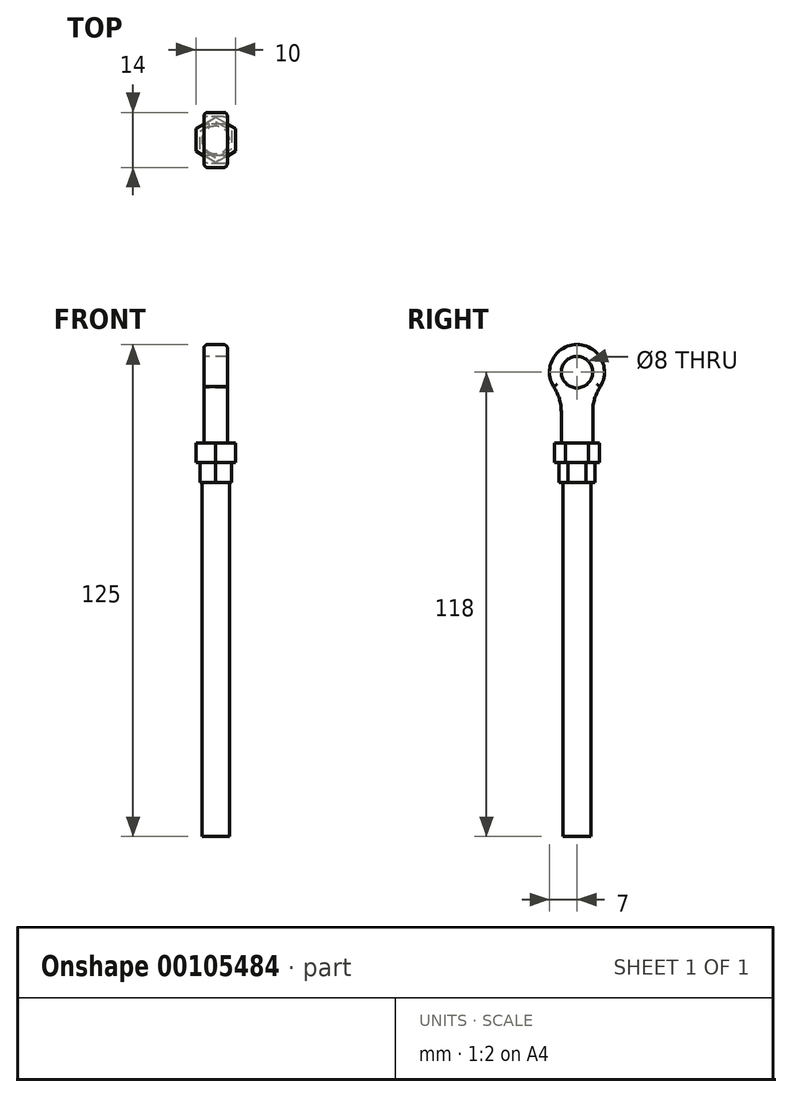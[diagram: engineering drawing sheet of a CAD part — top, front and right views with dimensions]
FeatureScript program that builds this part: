
annotation { "Feature Type Name" : "Feature", "Feature Type Description" : "" }
export const myFeature = defineFeature(function(context is Context, id is Id, definition is map)
    precondition{}
    {
        {
            var Q0;
            Q0=qCreatedBy(makeId("Top.planeOp"),FACE);
            var sketch = newSketch(context, id + "F0", { "sketchPlane" : qUnion([Q0])});
            skCircle(sketch, "E0", {"center": v(0, 0) * mm, "radius": 3.5 * mm});
            skSolve(sketch);
        }
        {
            var Q0;
            Q0=makeQuery(id+"F0.imprint","IMPRINT",FACE,{"disambiguationData":[TD([[makeQuery(id+"F0.imprint","IMPRINT",EDGE,{"derivedFrom":sQuery(id+"F0.wireOp",EDGE,"E0")}),1.0]])]});
            extrude(context, id + "F1", {"entities" : qUnion([Q0]), "depth" : 90 * mm});
        }
        {
            var Q0;
            Q0=makeQuery(id+"F1.opExtrude","CAP_FACE",FACE,{"disambiguationData":[OSD([sQuery(id+"F0.wireOp",EDGE,"E0")])],"isStart":false});
            var sketch = newSketch(context, id + "F2", { "sketchPlane" : qUnion([Q0])});
            skCircle(sketch, "E1.cCircle", {"center": v(0, 0) * mm, "radius": 4 * mm, "construction": true});
            skLineSegment(sketch, "E1.0", {"start": v(4, 2.3) * mm, "end": v(4, -2.3) * mm});
            skLineSegment(sketch, "E1.1", {"start": v(4, -2.3) * mm, "end": v(0, -4.62) * mm});
            skLineSegment(sketch, "E1.2", {"start": v(0, -4.62) * mm, "end": v(-4, -2.3) * mm});
            skLineSegment(sketch, "E1.3", {"start": v(-4, -2.3) * mm, "end": v(-4, 2.3) * mm});
            skLineSegment(sketch, "E1.4", {"start": v(-4, 2.3) * mm, "end": v(0, 4.62) * mm});
            skLineSegment(sketch, "E1.5", {"start": v(0, 4.62) * mm, "end": v(4, 2.3) * mm});
            skPoint(sketch, "E1.0.midPoint", {"position": v(4, 0) * mm});
            skSolve(sketch);
        }
        {
            var Q0;
            Q0 = qSketchRegion(id + "F2", true);
            extrude(context, id + "F3", {"entities" : qUnion([Q0]), "operationType" : NewBodyOperationType.ADD, "depth" : 5 * mm});
        }
        {
            var Q0;
            Q0=makeQuery(id+"F3.opExtrude","CAP_FACE",FACE,{"disambiguationData":[OSD([sQuery(id+"F2.wireOp",EDGE,"E1.0"),sQuery(id+"F2.wireOp",EDGE,"E1.1"),sQuery(id+"F2.wireOp",EDGE,"E1.2"),sQuery(id+"F2.wireOp",EDGE,"E1.3"),sQuery(id+"F2.wireOp",EDGE,"E1.4"),sQuery(id+"F2.wireOp",EDGE,"E1.5")])],"isStart":false});
            var sketch = newSketch(context, id + "F4", { "sketchPlane" : qUnion([Q0])});
            skCircle(sketch, "E2.cCircle", {"center": v(0, 0) * mm, "radius": 5 * mm, "construction": true});
            skLineSegment(sketch, "E2.0", {"start": v(5, 2.89) * mm, "end": v(5, -2.89) * mm});
            skLineSegment(sketch, "E2.1", {"start": v(5, -2.89) * mm, "end": v(0, -5.77) * mm});
            skLineSegment(sketch, "E2.2", {"start": v(0, -5.77) * mm, "end": v(-5, -2.89) * mm});
            skLineSegment(sketch, "E2.3", {"start": v(-5, -2.89) * mm, "end": v(-5, 2.89) * mm});
            skLineSegment(sketch, "E2.4", {"start": v(-5, 2.89) * mm, "end": v(0, 5.77) * mm});
            skLineSegment(sketch, "E2.5", {"start": v(0, 5.77) * mm, "end": v(5, 2.89) * mm});
            skPoint(sketch, "E2.0.midPoint", {"position": v(5, 0) * mm});
            skSolve(sketch);
        }
        {
            var Q0;
            Q0 = qSketchRegion(id + "F4", true);
            extrude(context, id + "F5", {"entities" : qUnion([Q0]), "operationType" : NewBodyOperationType.ADD, "depth" : 5 * mm});
        }
        {
            var Q0;
            Q0=qCreatedBy(makeId("Right.planeOp"),FACE);
            var sketch = newSketch(context, id + "F6", { "sketchPlane" : qUnion([Q0])});
            skLineSegment(sketch, "E3", {"start": v(0, 0) * mm, "end": v(0, 100) * mm});
            skArc(sketch, "E4", {"start": v(5.95, 114.3) * mm, "mid": v(0, 125) * mm, "end": v(-5.95, 114.3) * mm});
            skCircle(sketch, "E5", {"center": v(0, 118) * mm, "radius": 4 * mm});
            skLineSegment(sketch, "E6", {"start": v(0, 100) * mm, "end": v(-4, 100) * mm});
            skLineSegment(sketch, "E7", {"start": v(-4, 100) * mm, "end": v(-4, 108) * mm});
            skArc(sketch, "E8", {"start": v(-4, 108) * mm, "mid": v(-4.5, 111.3) * mm, "end": v(-5.95, 114.3) * mm});
            skArc(sketch, "E9.MirrorCS", {"start": v(4, 108) * mm, "mid": v(4.5, 111.3) * mm, "end": v(5.95, 114.3) * mm});
            skLineSegment(sketch, "E10.MirrorCS", {"start": v(4, 100) * mm, "end": v(4, 108) * mm});
            skLineSegment(sketch, "E11.MirrorCS", {"start": v(0, 100) * mm, "end": v(4, 100) * mm});
            skSolve(sketch);
        }
        {
            var Q0;
            Q0 = qSketchRegion(id + "F6", true);
            extrude(context, id + "F7", {"entities" : qUnion([Q0]), "operationType" : NewBodyOperationType.ADD, "endBound" : BoundingType.SYMMETRIC, "depth" : 6 * mm});
        }
        {
            var Q0;
            Q0=makeQuery(id+"F7.opExtrude","CAP_EDGE",EDGE,{"disambiguationData":[OSD([sQuery(id+"F6.wireOp",EDGE,"E8")])],"isStart":false});
            var Q1;
            Q1=makeQuery(id+"F7.opExtrude","CAP_EDGE",EDGE,{"disambiguationData":[OSD([sQuery(id+"F6.wireOp",EDGE,"E4")])],"isStart":false});
            var Q2;
            Q2=makeQuery(id+"F7.opExtrude","CAP_EDGE",EDGE,{"disambiguationData":[OSD([sQuery(id+"F6.wireOp",EDGE,"E9.MirrorCS")])],"isStart":false});
            var Q3;
            Q3=makeQuery(id+"F7.opExtrude","CAP_EDGE",EDGE,{"disambiguationData":[OSD([sQuery(id+"F6.wireOp",EDGE,"E9.MirrorCS")])],"isStart":true});
            var Q4;
            Q4=makeQuery(id+"F7.opExtrude","CAP_EDGE",EDGE,{"disambiguationData":[OSD([sQuery(id+"F6.wireOp",EDGE,"E8")])],"isStart":true});
            var Q5;
            Q5=makeQuery(id+"F7.opExtrude","CAP_EDGE",EDGE,{"disambiguationData":[OSD([sQuery(id+"F6.wireOp",EDGE,"E4")])],"isStart":true});
            fillet(context, id + "F8", {"entities" : qUnion([Q0, Q1, Q2, Q3, Q4, Q5]), "radius" : 1 * mm, "tangentPropagation" : true, "allowEdgeOverflow" : false});
        }
    });
